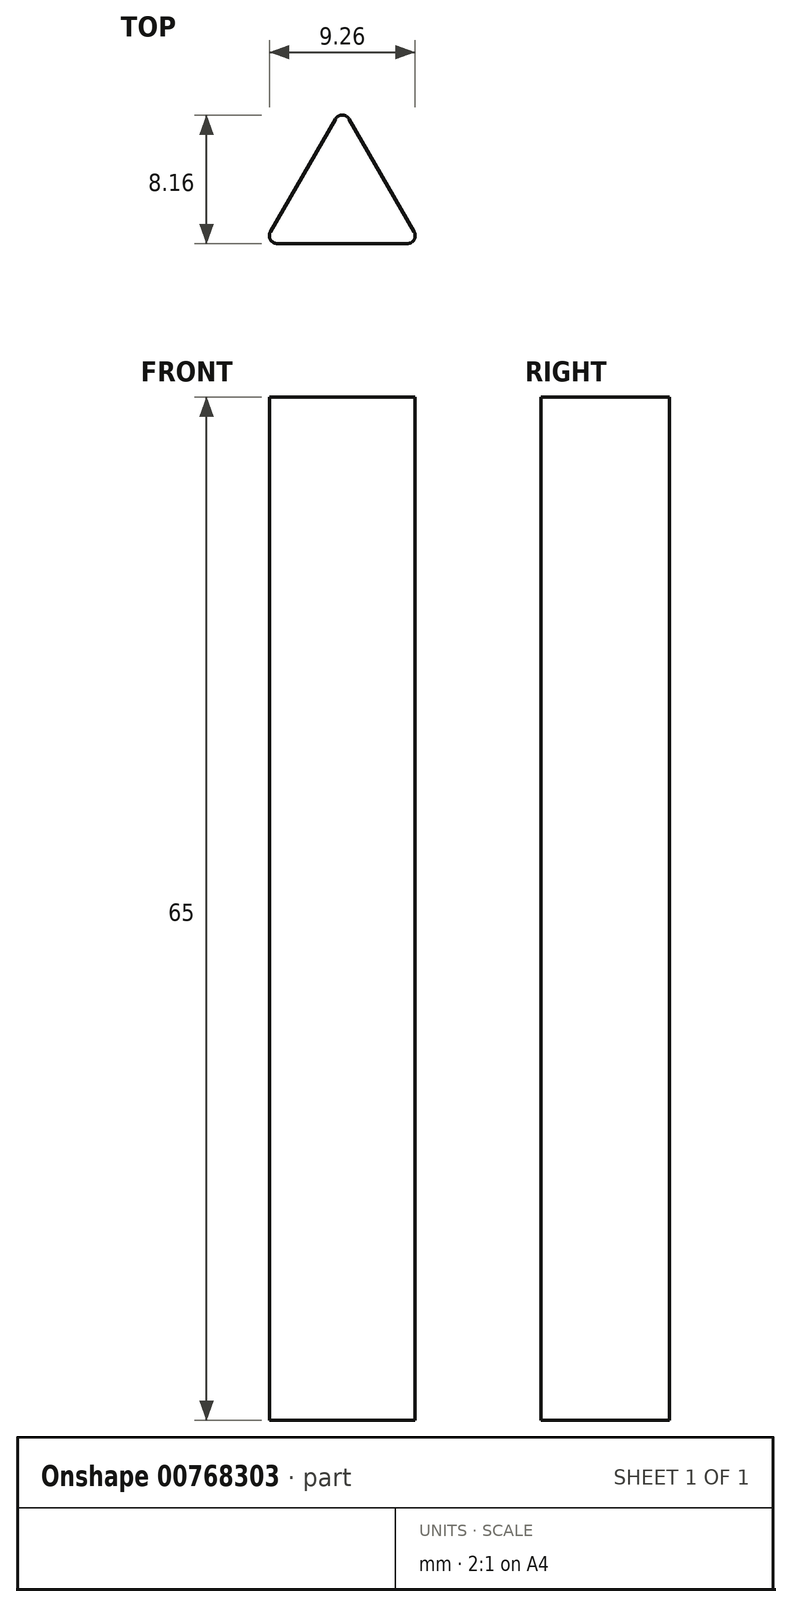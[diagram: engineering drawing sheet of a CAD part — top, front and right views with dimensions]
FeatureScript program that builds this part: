
annotation { "Feature Type Name" : "Feature", "Feature Type Description" : "" }
export const myFeature = defineFeature(function(context is Context, id is Id, definition is map)
    precondition{}
    {
        {
            var Q0;
            Q0=qCreatedBy(makeId("Top.planeOp"),FACE);
            var sketch = newSketch(context, id + "F0", { "sketchPlane" : qUnion([Q0])});
            skCircle(sketch, "E0.cCircle", {"center": v(0, 0) * mm, "radius": 5.77 * mm, "construction": true});
            skLineSegment(sketch, "E0.0", {"start": v(4.13, -2.89) * mm, "end": v(-4.13, -2.89) * mm});
            skLineSegment(sketch, "E0.1", {"start": v(-4.57, -2.14) * mm, "end": v(-0.43, 5.02) * mm});
            skLineSegment(sketch, "E0.2", {"start": v(0.43, 5.02) * mm, "end": v(4.57, -2.14) * mm});
            skPoint(sketch, "E1.visualSharp", {"position": v(0, 5.77) * mm});
            skArc(sketch, "E1.filletArc", {"start": v(0.43, 5.02) * mm, "mid": v(0, 5.27) * mm, "end": v(-0.43, 5.02) * mm});
            skPoint(sketch, "E2.visualSharp", {"position": v(5, -2.89) * mm});
            skArc(sketch, "E2.filletArc", {"start": v(4.13, -2.89) * mm, "mid": v(4.57, -2.64) * mm, "end": v(4.57, -2.14) * mm});
            skPoint(sketch, "E3.visualSharp", {"position": v(-5, -2.89) * mm});
            skArc(sketch, "E3.filletArc", {"start": v(-4.57, -2.14) * mm, "mid": v(-4.57, -2.64) * mm, "end": v(-4.13, -2.89) * mm});
            skSolve(sketch);
        }
        {
            var Q0;
            Q0=makeQuery(id+"F0.imprint","IMPRINT",FACE,{"disambiguationData":[TD([[makeQuery(id+"F0.imprint","IMPRINT",EDGE,{"derivedFrom":sQuery(id+"F0.wireOp",EDGE,"E0.0")}),-1.0]])]});
            extrude(context, id + "F1", {"entities" : qUnion([Q0]), "depth" : 65 * mm, "offsetDistance" : 25 * mm});
        }
    });
